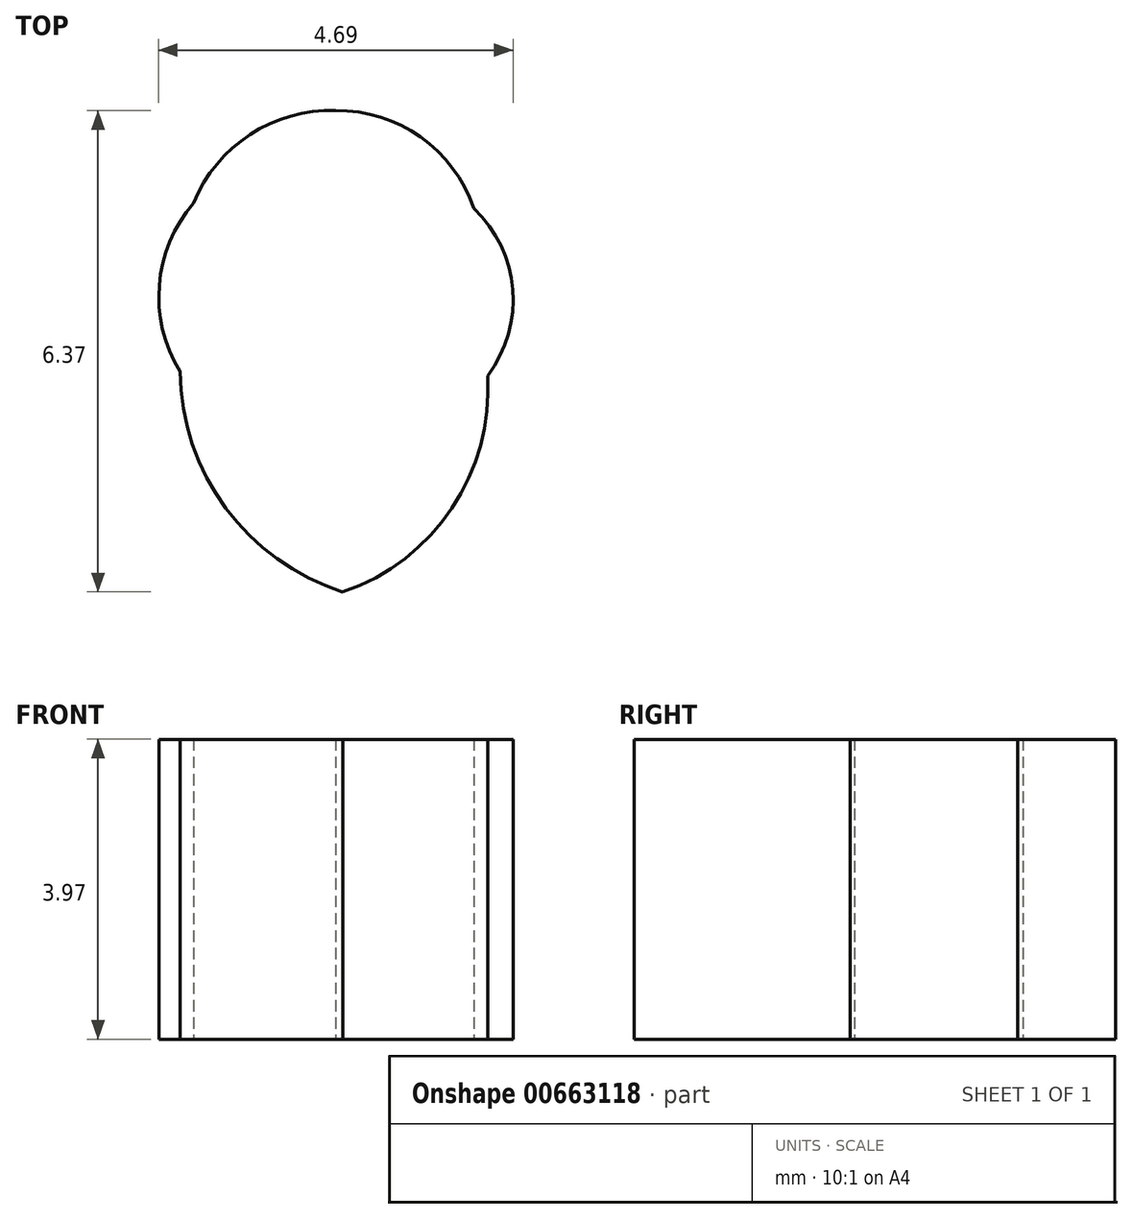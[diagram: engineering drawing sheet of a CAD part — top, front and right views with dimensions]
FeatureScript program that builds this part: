
annotation { "Feature Type Name" : "Feature", "Feature Type Description" : "" }
export const myFeature = defineFeature(function(context is Context, id is Id, definition is map)
    precondition{}
    {
        {
            var Q0;
            Q0=qCreatedBy(makeId("Top.planeOp"),FACE);
            var sketch = newSketch(context, id + "F0", { "sketchPlane" : qUnion([Q0])});
            skPoint(sketch, "E0.center", {"position": v(0, 0) * mm});
            skPoint(sketch, "E1.center", {"position": v(-0.03, 0.1) * mm});
            skLineSegment(sketch, "E2", {"start": v(7.76, 1.05) * mm, "end": v(7.76, 1.05) * mm});
            skLineSegment(sketch, "E3", {"start": v(8, -1.42) * mm, "end": v(8, -1.42) * mm});
            skLineSegment(sketch, "E4", {"start": v(6.33, 3.65) * mm, "end": v(6.36, 3.6) * mm});
            skArc(sketch, "E5", {"start": v(-2.16, -1.07) * mm, "mid": v(-1.55, -2.88) * mm, "end": v(0, -4) * mm});
            skArc(sketch, "E6", {"start": v(0, -4) * mm, "mid": v(1.44, -2.88) * mm, "end": v(1.91, -1.13) * mm});
            skArc(sketch, "E7", {"start": v(-0.1, 2.38) * mm, "mid": v(-1.23, 2.06) * mm, "end": v(-1.98, 1.16) * mm});
            skArc(sketch, "E8", {"start": v(-1.98, 1.16) * mm, "mid": v(-2.43, 0.07) * mm, "end": v(-2.16, -1.07) * mm});
            skArc(sketch, "E9", {"start": v(1.91, -1.13) * mm, "mid": v(2.24, 0.01) * mm, "end": v(1.73, 1.09) * mm});
            skArc(sketch, "E10", {"start": v(1.73, 1.09) * mm, "mid": v(1.03, 2.03) * mm, "end": v(-0.1, 2.38) * mm});
            skSolve(sketch);
        }
        {
            var Q0;
            Q0=makeQuery(id+"F0.imprint","IMPRINT",FACE,{"disambiguationData":[TD([[makeQuery(id+"F0.imprint","IMPRINT",EDGE,{"derivedFrom":sQuery(id+"F0.wireOp",EDGE,"E5")}),1.0]])]});
            extrude(context, id + "F1", {"entities" : qUnion([Q0]), "depth" : 3.97 * mm, "offsetDistance" : 25.4 * mm});
        }
    });
